FCSTD DOCUMENT  (FreeCAD 0.19R24366 (Git))
Label: button
License: All rights reserved
LicenseURL: http://en.wikipedia.org/wiki/All_rights_reserved
objects: Sketcher::SketchObject×1, PartDesign::Body×1
note: 2 computed .brp shape members not serialized (recipe doc carries the construction recipe); baked Part::Feature solids carry a one-line shape summary decoded from their .brp

FEATURE [Sketcher::SketchObject] Sketch
  FullyConstrained = false
  MapMode = 5
  Support = -> [XY_Plane]
  sketch-geometry (6):
    g0: LineSegment StartX=0 StartY=0 StartZ=0 EndX=-27 EndY=0 EndZ=0
    g1: LineSegment StartX=-27 StartY=0 StartZ=0 EndX=-27 EndY=22.605 EndZ=0
    g2: LineSegment StartX=-27 StartY=22.605 StartZ=0 EndX=-23.1933 EndY=22.605 EndZ=0
    g3: LineSegment StartX=-23.1933 StartY=22.605 StartZ=0 EndX=-23.1933 EndY=1.93278 EndZ=0
    g4: LineSegment StartX=-23.1933 StartY=1.93278 StartZ=0 EndX=0 EndY=1.93278 EndZ=0
    g5: LineSegment StartX=0 StartY=1.93278 StartZ=0 EndX=0 EndY=0 EndZ=0
  constraints (14):
    c: Coincident(g-1,g0)
    c: PointOnObject(g0,g-1)
    c: Coincident(g0,g1)
    c: Vertical(g1)
    c: Coincident(g1,g2)
    c: Coincident(g2,g3)
    c: Vertical(g3)
    c: Coincident(g3,g4)
    c: PointOnObject(g4,g-2)
    c: Horizontal(g4)
    c: Coincident(g4,g5)
    c: Coincident(g5,g0)
    c: Horizontal(g2)
    c: DistanceX(g0,g0) = 27
FEATURE [PartDesign::Body] Body
  Group = -> [Sketch]
  Origin = -> Origin
